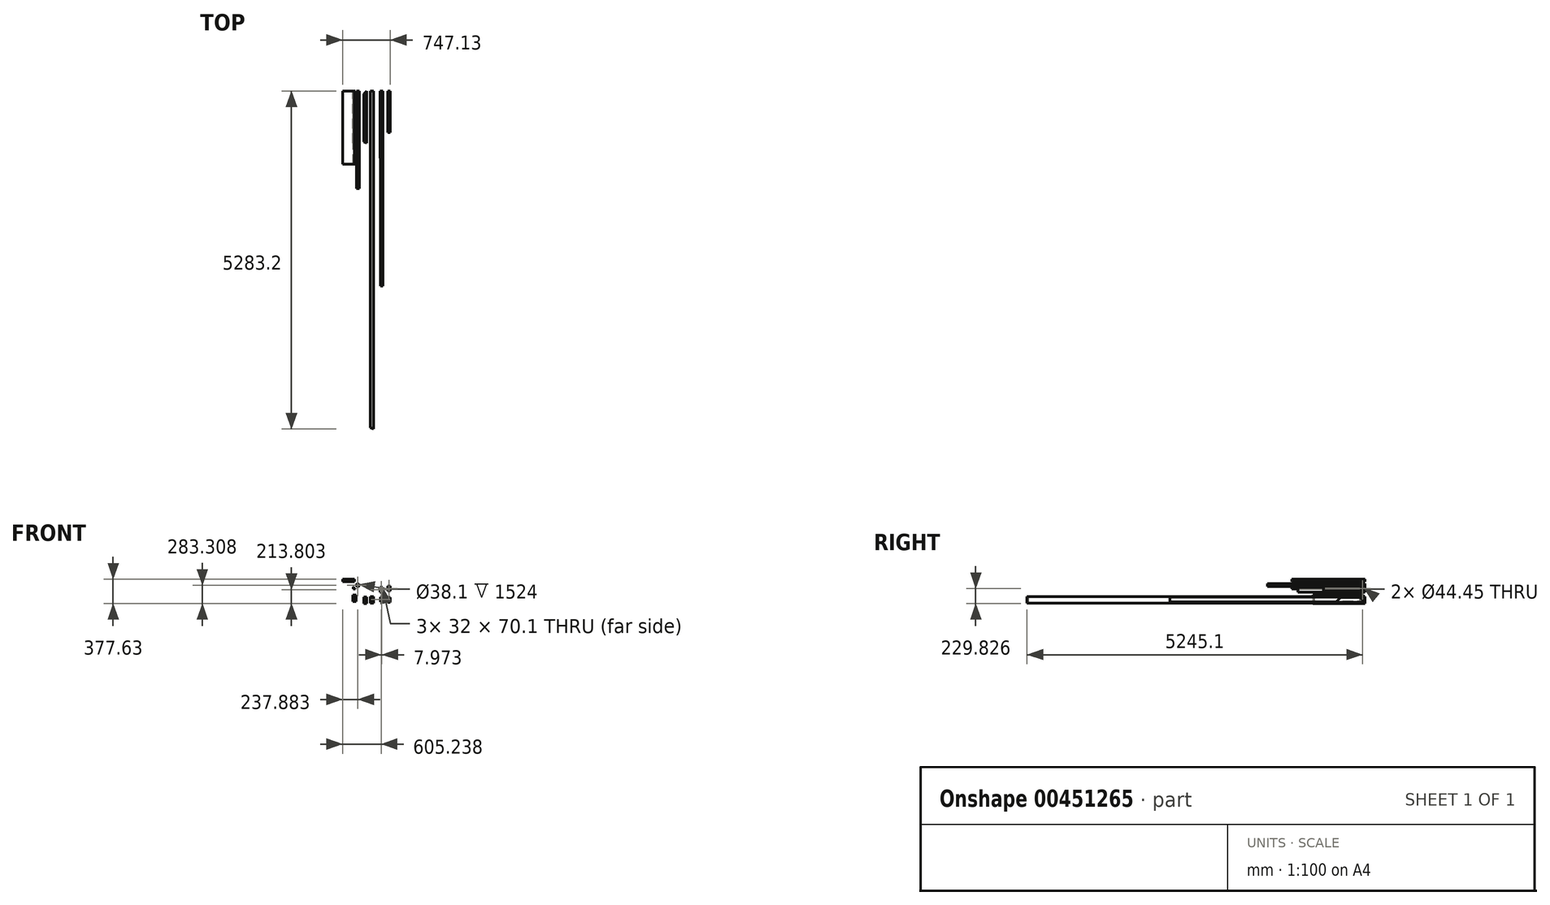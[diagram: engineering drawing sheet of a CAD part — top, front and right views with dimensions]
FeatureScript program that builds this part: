
annotation { "Feature Type Name" : "Feature", "Feature Type Description" : "" }
export const myFeature = defineFeature(function(context is Context, id is Id, definition is map)
    precondition{}
    {
        {
            var Q0;
            Q0=qCreatedBy(makeId("Front.planeOp"),FACE);
            var sketch = newSketch(context, id + "F0", { "sketchPlane" : qUnion([Q0])});
            skLineSegment(sketch, "E0.bottom", {"start": v(-47.75, 40.4) * mm, "end": v(3.05, 40.4) * mm});
            skLineSegment(sketch, "E0.top", {"start": v(-47.75, -61.2) * mm, "end": v(3.05, -61.2) * mm});
            skLineSegment(sketch, "E0.left", {"start": v(-47.75, 40.4) * mm, "end": v(-47.75, -61.2) * mm});
            skLineSegment(sketch, "E0.right", {"start": v(3.05, 40.4) * mm, "end": v(3.05, -61.2) * mm});
            skLineSegment(sketch, "E1.bottom", {"start": v(-44.7, 37.35) * mm, "end": v(0, 37.35) * mm});
            skLineSegment(sketch, "E1.top", {"start": v(-44.7, -58.15) * mm, "end": v(0, -58.15) * mm});
            skLineSegment(sketch, "E1.left", {"start": v(-44.7, 37.35) * mm, "end": v(-44.7, -58.15) * mm});
            skLineSegment(sketch, "E1.right", {"start": v(0, 37.35) * mm, "end": v(0, -58.15) * mm});
            skLineSegment(sketch, "E2.bottom", {"start": v(-154.32, 37.94) * mm, "end": v(-103.52, 37.94) * mm});
            skLineSegment(sketch, "E2.top", {"start": v(-154.32, -63.66) * mm, "end": v(-103.52, -63.66) * mm});
            skLineSegment(sketch, "E2.left", {"start": v(-154.32, 37.94) * mm, "end": v(-154.32, -63.66) * mm});
            skLineSegment(sketch, "E2.right", {"start": v(-103.52, 37.94) * mm, "end": v(-103.52, -63.66) * mm});
            skLineSegment(sketch, "E3.bottom", {"start": v(-151.28, 34.89) * mm, "end": v(-106.57, 34.89) * mm});
            skLineSegment(sketch, "E3.top", {"start": v(-151.28, -60.62) * mm, "end": v(-106.57, -60.62) * mm});
            skLineSegment(sketch, "E3.left", {"start": v(-151.28, 34.89) * mm, "end": v(-151.28, -60.62) * mm});
            skLineSegment(sketch, "E3.right", {"start": v(-106.57, 34.89) * mm, "end": v(-106.57, -60.62) * mm});
            skLineSegment(sketch, "E4.bottom", {"start": v(110.97, 35.91) * mm, "end": v(149.07, 35.91) * mm});
            skLineSegment(sketch, "E4.top", {"start": v(110.97, -40.29) * mm, "end": v(149.07, -40.29) * mm});
            skLineSegment(sketch, "E4.left", {"start": v(110.97, 35.91) * mm, "end": v(110.97, -40.29) * mm});
            skLineSegment(sketch, "E4.right", {"start": v(149.07, 35.91) * mm, "end": v(149.07, -40.29) * mm});
            skLineSegment(sketch, "E5.bottom", {"start": v(114.02, 32.87) * mm, "end": v(146.02, 32.87) * mm});
            skLineSegment(sketch, "E5.top", {"start": v(114.02, -37.24) * mm, "end": v(146.02, -37.24) * mm});
            skLineSegment(sketch, "E5.left", {"start": v(114.02, 32.87) * mm, "end": v(114.02, -37.24) * mm});
            skLineSegment(sketch, "E5.right", {"start": v(146.02, 32.87) * mm, "end": v(146.02, -37.24) * mm});
            skLineSegment(sketch, "E6.bottom", {"start": v(103, 188.24) * mm, "end": v(141.1, 188.24) * mm});
            skLineSegment(sketch, "E6.top", {"start": v(103, 112.04) * mm, "end": v(141.1, 112.04) * mm});
            skLineSegment(sketch, "E6.left", {"start": v(103, 188.24) * mm, "end": v(103, 112.04) * mm});
            skLineSegment(sketch, "E6.right", {"start": v(141.1, 188.24) * mm, "end": v(141.1, 112.04) * mm});
            skLineSegment(sketch, "E7.bottom", {"start": v(106.05, 185.2) * mm, "end": v(138.05, 185.2) * mm});
            skLineSegment(sketch, "E7.top", {"start": v(106.05, 115.1) * mm, "end": v(138.05, 115.1) * mm});
            skLineSegment(sketch, "E7.left", {"start": v(106.05, 185.2) * mm, "end": v(106.05, 115.1) * mm});
            skLineSegment(sketch, "E7.right", {"start": v(138.05, 185.2) * mm, "end": v(138.05, 115.1) * mm});
            skLineSegment(sketch, "E8.bottom", {"start": v(221.16, 204.27) * mm, "end": v(259.26, 204.27) * mm});
            skLineSegment(sketch, "E8.top", {"start": v(221.16, 128.07) * mm, "end": v(259.26, 128.07) * mm});
            skLineSegment(sketch, "E8.left", {"start": v(221.16, 204.27) * mm, "end": v(221.16, 128.07) * mm});
            skLineSegment(sketch, "E8.right", {"start": v(259.26, 204.27) * mm, "end": v(259.26, 128.07) * mm});
            skLineSegment(sketch, "E9.bottom", {"start": v(224.21, 201.22) * mm, "end": v(256.21, 201.22) * mm});
            skLineSegment(sketch, "E9.top", {"start": v(224.21, 131.11) * mm, "end": v(256.21, 131.11) * mm});
            skLineSegment(sketch, "E9.left", {"start": v(224.21, 201.22) * mm, "end": v(224.21, 131.11) * mm});
            skLineSegment(sketch, "E9.right", {"start": v(256.21, 201.22) * mm, "end": v(256.21, 131.11) * mm});
            skLineSegment(sketch, "E10.bottom", {"start": v(225.84, 30.69) * mm, "end": v(263.94, 30.69) * mm});
            skLineSegment(sketch, "E10.top", {"start": v(225.84, -45.51) * mm, "end": v(263.94, -45.51) * mm});
            skLineSegment(sketch, "E10.left", {"start": v(225.84, 30.69) * mm, "end": v(225.84, -45.51) * mm});
            skLineSegment(sketch, "E10.right", {"start": v(263.94, 30.69) * mm, "end": v(263.94, -45.51) * mm});
            skLineSegment(sketch, "E11.bottom", {"start": v(228.88, 27.64) * mm, "end": v(260.89, 27.64) * mm});
            skLineSegment(sketch, "E11.top", {"start": v(228.88, -42.46) * mm, "end": v(260.89, -42.46) * mm});
            skLineSegment(sketch, "E11.left", {"start": v(228.88, 27.64) * mm, "end": v(228.88, -42.46) * mm});
            skLineSegment(sketch, "E11.right", {"start": v(260.89, 27.64) * mm, "end": v(260.89, -42.46) * mm});
            skLineSegment(sketch, "E12", {"start": v(-315.23, 194.58) * mm, "end": v(-315.23, 162.83) * mm});
            skLineSegment(sketch, "E13", {"start": v(-315.23, 162.83) * mm, "end": v(-283.48, 162.83) * mm});
            skLineSegment(sketch, "E14", {"start": v(-283.48, 162.83) * mm, "end": v(-283.48, 166) * mm});
            skLineSegment(sketch, "E15", {"start": v(-283.48, 166) * mm, "end": v(-312.05, 166) * mm});
            skLineSegment(sketch, "E16", {"start": v(-312.05, 166) * mm, "end": v(-312.05, 194.58) * mm});
            skLineSegment(sketch, "E17", {"start": v(-312.05, 194.58) * mm, "end": v(-315.23, 194.58) * mm});
            skCircle(sketch, "E18", {"center": v(-245.3, 219.65) * mm, "radius": 22.23 * mm});
            skCircle(sketch, "E19", {"center": v(-245.3, 219.65) * mm, "radius": 19.05 * mm});
            skLineSegment(sketch, "E20.bottom", {"start": v(-483.19, 313.97) * mm, "end": v(-299.04, 313.97) * mm});
            skLineSegment(sketch, "E20.top", {"start": v(-483.19, 275.87) * mm, "end": v(-299.04, 275.87) * mm});
            skLineSegment(sketch, "E20.left", {"start": v(-483.19, 313.97) * mm, "end": v(-483.19, 275.87) * mm});
            skLineSegment(sketch, "E20.right", {"start": v(-299.04, 313.97) * mm, "end": v(-299.04, 275.87) * mm});
            skLineSegment(sketch, "E21.bottom", {"start": v(-325.22, 68.03) * mm, "end": v(-274.42, 68.03) * mm});
            skLineSegment(sketch, "E21.top", {"start": v(-325.22, -33.57) * mm, "end": v(-274.42, -33.57) * mm});
            skLineSegment(sketch, "E21.left", {"start": v(-325.22, 68.03) * mm, "end": v(-325.22, -33.57) * mm});
            skLineSegment(sketch, "E21.right", {"start": v(-274.42, 68.03) * mm, "end": v(-274.42, -33.57) * mm});
            skLineSegment(sketch, "E22.bottom", {"start": v(-322.18, 64.98) * mm, "end": v(-277.47, 64.98) * mm});
            skLineSegment(sketch, "E22.top", {"start": v(-322.18, -30.52) * mm, "end": v(-277.47, -30.52) * mm});
            skLineSegment(sketch, "E22.left", {"start": v(-322.18, 64.98) * mm, "end": v(-322.18, -30.52) * mm});
            skLineSegment(sketch, "E22.right", {"start": v(-277.47, 64.98) * mm, "end": v(-277.47, -30.52) * mm});
            skSolve(sketch);
        }
        {
            var Q0;
            Q0=makeQuery(id+"F0.imprint","IMPRINT",FACE,{"disambiguationData":[TD([[makeQuery(id+"F0.imprint","IMPRINT",EDGE,{"derivedFrom":sQuery(id+"F0.wireOp",EDGE,"E20.bottom")}),-1.0]])]});
            extrude(context, id + "F1", {"entities" : qUnion([Q0]), "depth" : 1143 * mm});
        }
        {
            var Q0;
            Q0=makeQuery(id+"F0.imprint","IMPRINT",FACE,{"disambiguationData":[TD([[makeQuery(id+"F0.imprint","IMPRINT",EDGE,{"derivedFrom":sQuery(id+"F0.wireOp",EDGE,"E18")}),1.0]])]});
            extrude(context, id + "F2", {"entities" : qUnion([Q0]), "depth" : 1524 * mm});
        }
        {
            var Q0;
            Q0=makeQuery(id+"F0.imprint","IMPRINT",FACE,{"disambiguationData":[TD([[makeQuery(id+"F0.imprint","IMPRINT",EDGE,{"derivedFrom":sQuery(id+"F0.wireOp",EDGE,"E12")}),1.0]])]});
            extrude(context, id + "F3", {"entities" : qUnion([Q0]), "depth" : 1143 * mm});
        }
        {
            var Q0;
            Q0=makeQuery(id+"F0.imprint","IMPRINT",FACE,{"disambiguationData":[TD([[makeQuery(id+"F0.imprint","IMPRINT",EDGE,{"derivedFrom":sQuery(id+"F0.wireOp",EDGE,"E2.bottom")}),-1.0]])]});
            extrude(context, id + "F4", {"entities" : qUnion([Q0]), "depth" : 812.8 * mm});
        }
        {
            var Q0;
            Q0=makeQuery(id+"F0.imprint","IMPRINT",FACE,{"disambiguationData":[TD([[makeQuery(id+"F0.imprint","IMPRINT",EDGE,{"derivedFrom":sQuery(id+"F0.wireOp",EDGE,"E0.bottom")}),-1.0]])]});
            extrude(context, id + "F5", {"entities" : qUnion([Q0]), "depth" : 5283.2 * mm});
        }
        {
            var Q0;
            Q0=makeQuery(id+"F0.imprint","IMPRINT",FACE,{"disambiguationData":[TD([[makeQuery(id+"F0.imprint","IMPRINT",EDGE,{"derivedFrom":sQuery(id+"F0.wireOp",EDGE,"E6.bottom")}),-1.0]])]});
            extrude(context, id + "F6", {"entities" : qUnion([Q0]), "depth" : 1047.75 * mm});
        }
        {
            var Q0;
            Q0=makeQuery(id+"F0.imprint","IMPRINT",FACE,{"disambiguationData":[TD([[makeQuery(id+"F0.imprint","IMPRINT",EDGE,{"derivedFrom":sQuery(id+"F0.wireOp",EDGE,"E4.bottom")}),-1.0]])]});
            extrude(context, id + "F7", {"entities" : qUnion([Q0]), "depth" : 3048 * mm});
        }
        {
            var Q0;
            Q0=makeQuery(id+"F0.imprint","IMPRINT",FACE,{"disambiguationData":[TD([[makeQuery(id+"F0.imprint","IMPRINT",EDGE,{"derivedFrom":sQuery(id+"F0.wireOp",EDGE,"E8.bottom")}),-1.0]])]});
            extrude(context, id + "F8", {"entities" : qUnion([Q0]), "depth" : 647.7 * mm});
        }
        {
            var Q0;
            Q0=makeQuery(id+"F0.imprint","IMPRINT",FACE,{"disambiguationData":[TD([[makeQuery(id+"F0.imprint","IMPRINT",EDGE,{"derivedFrom":sQuery(id+"F0.wireOp",EDGE,"E10.bottom")}),-1.0]])]});
            extrude(context, id + "F9", {"entities" : qUnion([Q0]), "depth" : 457.2 * mm});
        }
        {
            var Q0;
            Q0=makeQuery(id+"F4.opExtrude","SWEPT_FACE",FACE,{"disambiguationData":[OSD([sQuery(id+"F0.wireOp",EDGE,"E2.bottom")])]});
            var sketch = newSketch(context, id + "F10", { "sketchPlane" : qUnion([Q0])});
            skLineSegment(sketch, "E23", {"start": v(-103.52, -812.8) * mm, "end": v(-154.32, -791.76) * mm});
            skLineSegment(sketch, "E24", {"start": v(-103.52, 0) * mm, "end": v(-154.32, -50.8) * mm});
            skLineSegment(sketch, "E25", {"start": v(-154.32, -77.74) * mm, "end": v(-103.52, -26.94) * mm});
            skSolve(sketch);
        }
        {
            var Q0;
            Q0=makeQuery(id+"F5.opExtrude","SWEPT_FACE",FACE,{"disambiguationData":[OSD([sQuery(id+"F0.wireOp",EDGE,"E0.bottom")])]});
            var sketch = newSketch(context, id + "F11", { "sketchPlane" : qUnion([Q0])});
            skLineSegment(sketch, "E26", {"start": v(3.05, -5283.2) * mm, "end": v(-47.75, -5262.16) * mm});
            skSolve(sketch);
        }
        {
            var Q0;
            Q0=makeQuery(id+"F8.opExtrude","SWEPT_FACE",FACE,{"disambiguationData":[OSD([sQuery(id+"F0.wireOp",EDGE,"E8.right")])]});
            var sketch = newSketch(context, id + "F12", { "sketchPlane" : qUnion([Q0])});
            skCircle(sketch, "E27", {"center": v(-38.1, 166.17) * mm, "radius": 22.23 * mm});
            skSolve(sketch);
        }
        {
            var Q0;
            Q0=makeQuery(id+"F12.imprint","IMPRINT",FACE,{"disambiguationData":[TD([[makeQuery(id+"F12.imprint","IMPRINT",EDGE,{"derivedFrom":sQuery(id+"F12.wireOp",EDGE,"E27")}),1.0]])]});
            extrude(context, id + "F13", {"entities" : qUnion([Q0]), "operationType" : NewBodyOperationType.REMOVE, "oppositeDirection" : true, "depth" : 38.1 * mm});
        }
        {
            var Q0;
            Q0=makeQuery(id+"F9.opExtrude","SWEPT_FACE",FACE,{"disambiguationData":[OSD([sQuery(id+"F0.wireOp",EDGE,"E10.right")])]});
            var sketch = newSketch(context, id + "F14", { "sketchPlane" : qUnion([Q0])});
            skLineSegment(sketch, "E28", {"start": v(-457.2, -45.51) * mm, "end": v(-381, 30.69) * mm});
            skLineSegment(sketch, "E29", {"start": v(0, -45.51) * mm, "end": v(-76.2, 30.69) * mm});
            skSolve(sketch);
        }
        {
            var Q0;
            {var subQ0=sQuery(id+"F14.wireOp",EDGE,"E28");Q0=makeQuery(id+"F14.imprint","IMPRINT",FACE,{"disambiguationData":[TD([[makeQuery(id+"F14.imprint","IMPRINT",EDGE,{"derivedFrom":subQ0}),1.0]])]});}
            var Q1;
            {var subQ0=sQuery(id+"F14.wireOp",EDGE,"E29");Q1=makeQuery(id+"F14.imprint","IMPRINT",FACE,{"disambiguationData":[TD([[makeQuery(id+"F14.imprint","IMPRINT",EDGE,{"derivedFrom":subQ0}),-1.0]])]});}
            extrude(context, id + "F15", {"entities" : qUnion([Q0, Q1]), "operationType" : NewBodyOperationType.REMOVE, "oppositeDirection" : true, "depth" : 38.1 * mm});
        }
        {
            var Q0;
            {var subQ0=sQuery(id+"F10.wireOp",EDGE,"E24");Q0=makeQuery(id+"F10.imprint","IMPRINT",FACE,{"disambiguationData":[TD([[makeQuery(id+"F10.imprint","IMPRINT",EDGE,{"derivedFrom":subQ0}),-1.0]])]});}
            extrude(context, id + "F16", {"entities" : qUnion([Q0]), "operationType" : NewBodyOperationType.REMOVE, "oppositeDirection" : true, "depth" : 101.6 * mm});
        }
        {
            var Q0;
            {var subQ0=sQuery(id+"F10.wireOp",EDGE,"E24");Q0=makeQuery(id+"F10.imprint","IMPRINT",FACE,{"disambiguationData":[TD([[makeQuery(id+"F10.imprint","IMPRINT",EDGE,{"derivedFrom":subQ0}),1.0]])]});}
            extrude(context, id + "F17", {"entities" : qUnion([Q0]), "operationType" : NewBodyOperationType.REMOVE, "oppositeDirection" : true, "depth" : 76.2 * mm});
        }
        {
            var Q0;
            {var subQ0=sQuery(id+"F10.wireOp",EDGE,"E23");Q0=makeQuery(id+"F10.imprint","IMPRINT",FACE,{"disambiguationData":[TD([[makeQuery(id+"F10.imprint","IMPRINT",EDGE,{"derivedFrom":subQ0}),1.0]])]});}
            extrude(context, id + "F18", {"entities" : qUnion([Q0]), "operationType" : NewBodyOperationType.REMOVE, "oppositeDirection" : true, "depth" : 101.6 * mm});
        }
        {
            var Q0;
            {var subQ0=sQuery(id+"F11.wireOp",EDGE,"E26");Q0=makeQuery(id+"F11.imprint","IMPRINT",FACE,{"disambiguationData":[TD([[makeQuery(id+"F11.imprint","IMPRINT",EDGE,{"derivedFrom":subQ0}),1.0]])]});}
            extrude(context, id + "F19", {"entities" : qUnion([Q0]), "operationType" : NewBodyOperationType.REMOVE, "oppositeDirection" : true, "depth" : 101.6 * mm});
        }
        {
            var Q0;
            Q0=makeQuery(id+"F0.imprint","IMPRINT",FACE,{"disambiguationData":[TD([[makeQuery(id+"F0.imprint","IMPRINT",EDGE,{"derivedFrom":sQuery(id+"F0.wireOp",EDGE,"E21.bottom")}),-1.0]])]});
            extrude(context, id + "F20", {"entities" : qUnion([Q0]), "depth" : 812.8 * mm});
        }
        {
            var Q0;
            Q0=makeQuery(id+"F20.opExtrude","SWEPT_FACE",FACE,{"disambiguationData":[OSD([sQuery(id+"F0.wireOp",EDGE,"E21.bottom")])]});
            var sketch = newSketch(context, id + "F21", { "sketchPlane" : qUnion([Q0])});
            skLineSegment(sketch, "E30", {"start": v(-325.22, -812.8) * mm, "end": v(-274.42, -791.76) * mm});
            skLineSegment(sketch, "E31", {"start": v(-325.22, 0) * mm, "end": v(-274.42, -50.8) * mm});
            skLineSegment(sketch, "E32", {"start": v(-325.22, -26.94) * mm, "end": v(-274.42, -77.74) * mm});
            skSolve(sketch);
        }
        {
            var Q0;
            {var subQ0=sQuery(id+"F21.wireOp",EDGE,"E30");Q0=makeQuery(id+"F21.imprint","IMPRINT",FACE,{"disambiguationData":[TD([[makeQuery(id+"F21.imprint","IMPRINT",EDGE,{"derivedFrom":subQ0}),-1.0]])]});}
            var Q1;
            {var subQ0=sQuery(id+"F21.wireOp",EDGE,"E31");Q1=makeQuery(id+"F21.imprint","IMPRINT",FACE,{"disambiguationData":[TD([[makeQuery(id+"F21.imprint","IMPRINT",EDGE,{"derivedFrom":subQ0}),1.0]])]});}
            extrude(context, id + "F22", {"entities" : qUnion([Q0, Q1]), "operationType" : NewBodyOperationType.REMOVE, "oppositeDirection" : true, "depth" : 101.6 * mm});
        }
        {
            var Q0;
            {var subQ0=sQuery(id+"F21.wireOp",EDGE,"E31");Q0=makeQuery(id+"F21.imprint","IMPRINT",FACE,{"disambiguationData":[TD([[makeQuery(id+"F21.imprint","IMPRINT",EDGE,{"derivedFrom":subQ0}),-1.0]])]});}
            extrude(context, id + "F23", {"entities" : qUnion([Q0]), "operationType" : NewBodyOperationType.REMOVE, "oppositeDirection" : true, "depth" : 76.2 * mm});
        }
    });
